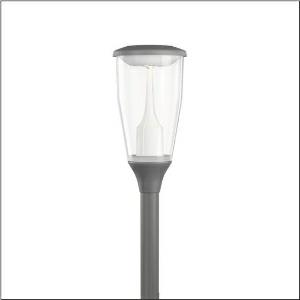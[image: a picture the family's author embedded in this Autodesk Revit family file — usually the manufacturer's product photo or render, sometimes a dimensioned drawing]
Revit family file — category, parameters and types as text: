
# Revit family: dl_11_iq___st1_2a_5xa5575af14h000022_aeb9
name_source: partatom
category: Lighting Fixtures
units: mm (PartAtom-declared; Revit-internal decimal feet)

## family parameters
Cut with Voids When Loaded = No
Host = Face
Light Source = No
Part Type = Normal
Room Calculation Point = No
Round Connector Dimension = Use Diameter
Shared = No

## types (1)
- --- (1 x LED, 1560 lm, 12.9 W, 2200K)
    Apparent Load = 13 VA
    CIE Flux Codes = 24 63 94 96 100
    Color Rendering = 70
    Color Temperature = 2200K
    Default Elevation = 1800 mm
    Description = DL 11 iQ, mast luminaire, Module 540 iQ-SR, primary light control with 3 zone facetted reflector, of plastic, silver coated, highly specular, structured, primary optical cover: cover, of PMMA, transparent, light distribution: ST1.2a, light emission: direct distribution, primary light characteristic: asymmetric, installation type: post-top, LED, High Power LED, rated luminous flux: 1.560lm, luminous efficacy: 149lm/W, light colour: 722, colour temperature: 2200K, control gear: iQ Street-Remote, control: Street-Remote, Auto-Match, Temp-Guard, Lumen-Switch, Night-Set, Smart-Wire, Light-Fading, Desk-Remote (wireless, voltage-free reading and setting of iQ features in the workshop via application-optimized NFC function/RFID function), optimised constant luminous flux control (CLO 2.0), mains connection: 220..240V, AC, 50/60Hz, connection cable pre-assembled, cable length: 5,5m, wiring characteristics: H07RN-F, 5-core, 1.5mm², start of lifetime: 13W, end of service life: 13W, reduction: 5W, luminaire housing, upper part, of diecast aluminium, coated, Siteco® metallic grey (DB 702S), spigot size: 76mm (post-top), mounting height: 3..5m, post-top mast mounting element, of diecast aluminium, coated, Siteco® metallic grey (DB 702S), Module 540 iQ-SR, traffic white (RAL 9016), equipment: standard, protection rating (complete): IP66, insulation class (complete): insulation class II (safety insulation), certification: CE, ENEC, ENEC+, VDE, impact resistance: IK07, packaging unit: 1 piece

Light Distribution: ST1.2a
    Height = 665 mm
    Lamp = 1 x LED
    Lamp Light Flux = 1560 lm
    Lamp Power = 12.9 W
    Lamp count = 1
    Length = 334 mm
    Luminous efficacy = 121 lm/W
    Manufacturer = Siteco
    ModVariant = No
    Model = 5XA5575AF14H000022
    Number of Poles = 1
    OnlyDefault = Yes
    Power Factor = 1
    Product Name = DL 11 iQ | ST1.2a
    Product group = mast luminaire | pylon top
    ProductGroupID = 6100
    Protection Class = Protection class II
    Protection Degree = IP 66
    RLX_Detail_Level = 1
    RLX_Emergency_Light_Flux = 0 lm
    RLX_Emergency_Type = 0
    RLX_Emergency_Type_DB = No
    RlxData = <blob elided: 153893 chars, md5=00d6ec15>
    Socket = socket
    Standby Power = 0 W
    System Light Flux = 1560 lm
    System Power = 13 W
    Type Comments = factory setting: luminous flux: 100 % | dim-lin: 254 | 516 mA
    Type Image = l_1258354.jpg
    URL = http://relux.com
    VarID = @adj_094928
    Voltage = 0 V
    Weight = 0.00 kg
    Width = 0 mm  [stored 0 ft]

note: [stored X ft] marks values corroborated as IEEE doubles in the binary element streams (Revit-internal decimal feet)

## geometry (parser evidence)
native form markers: Blend x4, Sweep x11
no freeform markers — native parametric forms only
